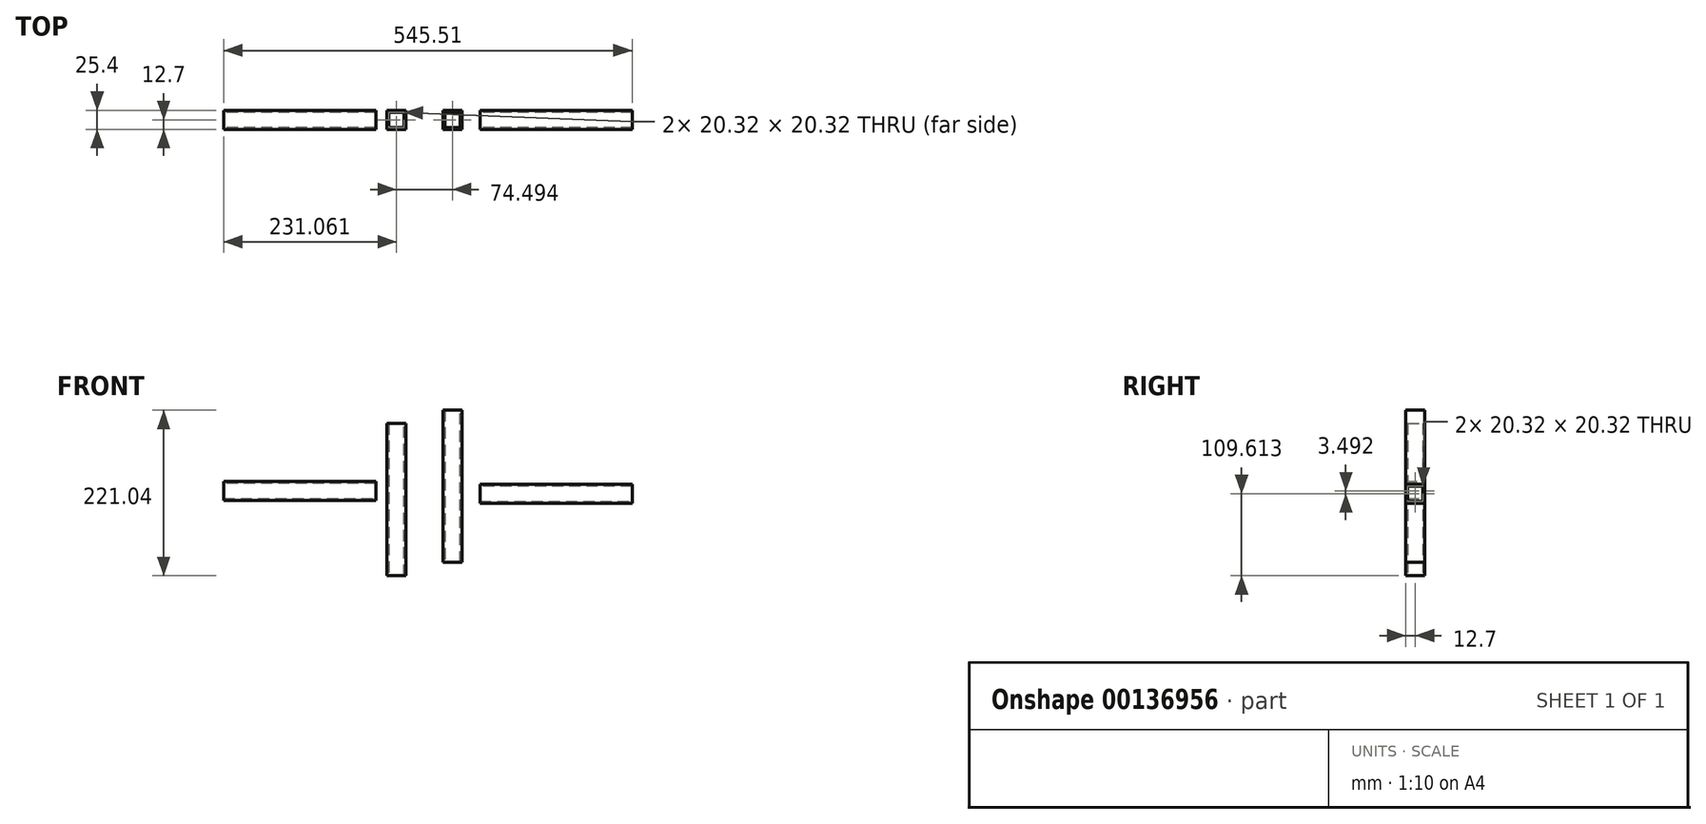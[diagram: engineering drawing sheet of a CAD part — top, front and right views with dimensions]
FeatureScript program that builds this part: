
annotation { "Feature Type Name" : "Feature", "Feature Type Description" : "" }
export const myFeature = defineFeature(function(context is Context, id is Id, definition is map)
    precondition{}
    {
        {
            var Q0;
            Q0=qCreatedBy(makeId("Front.planeOp"),FACE);
            var sketch = newSketch(context, id + "F0", { "sketchPlane" : qUnion([Q0])});
            skLineSegment(sketch, "E0", {"start": v(-59.04, 109.04) * mm, "end": v(-59.04, -94.16) * mm});
            skLineSegment(sketch, "E1", {"start": v(-59.04, -94.16) * mm, "end": v(-33.64, -94.16) * mm});
            skLineSegment(sketch, "E2", {"start": v(-33.64, -94.16) * mm, "end": v(-33.64, 109.04) * mm});
            skLineSegment(sketch, "E3", {"start": v(-33.64, 109.04) * mm, "end": v(-59.04, 109.04) * mm});
            skLineSegment(sketch, "E4", {"start": v(15.46, 126.88) * mm, "end": v(15.46, -76.32) * mm});
            skLineSegment(sketch, "E5", {"start": v(15.46, -76.32) * mm, "end": v(40.86, -76.32) * mm});
            skLineSegment(sketch, "E6", {"start": v(40.86, -76.32) * mm, "end": v(40.86, 126.88) * mm});
            skLineSegment(sketch, "E7", {"start": v(40.86, 126.88) * mm, "end": v(15.46, 126.88) * mm});
            skLineSegment(sketch, "E8", {"start": v(268.1, 28.15) * mm, "end": v(64.9, 28.15) * mm});
            skLineSegment(sketch, "E9", {"start": v(64.9, 28.15) * mm, "end": v(64.9, 2.75) * mm});
            skLineSegment(sketch, "E10", {"start": v(64.9, 2.75) * mm, "end": v(268.1, 2.75) * mm});
            skLineSegment(sketch, "E11", {"start": v(268.1, 28.15) * mm, "end": v(268.1, 2.75) * mm});
            skLineSegment(sketch, "E12", {"start": v(-74.2, 31.65) * mm, "end": v(-277.4, 31.65) * mm});
            skLineSegment(sketch, "E13", {"start": v(-277.4, 31.65) * mm, "end": v(-277.4, 6.25) * mm});
            skLineSegment(sketch, "E14", {"start": v(-277.4, 6.25) * mm, "end": v(-74.2, 6.25) * mm});
            skLineSegment(sketch, "E15", {"start": v(-74.2, 31.65) * mm, "end": v(-74.2, 6.25) * mm});
            skSolve(sketch);
        }
        {
            var Q0;
            Q0 = qSketchRegion(id + "F0", true);
            extrude(context, id + "F1", {"entities" : qUnion([Q0]), "depth" : 25.4 * mm});
        }
        {
            var Q0;
            Q0=makeQuery(id+"F1.opExtrude","SWEPT_FACE",FACE,{"disambiguationData":[OSD([sQuery(id+"F0.wireOp",EDGE,"E7")])]});
            var Q1;
            Q1=makeQuery(id+"F1.opExtrude","SWEPT_FACE",FACE,{"disambiguationData":[OSD([sQuery(id+"F0.wireOp",EDGE,"E3")])]});
            var Q2;
            Q2=makeQuery(id+"F1.opExtrude","SWEPT_FACE",FACE,{"disambiguationData":[OSD([sQuery(id+"F0.wireOp",EDGE,"E15")])]});
            var Q3;
            Q3=makeQuery(id+"F1.opExtrude","SWEPT_FACE",FACE,{"disambiguationData":[OSD([sQuery(id+"F0.wireOp",EDGE,"E11")])]});
            var Q4;
            Q4=makeQuery(id+"F1.opExtrude","SWEPT_FACE",FACE,{"disambiguationData":[OSD([sQuery(id+"F0.wireOp",EDGE,"E1")])]});
            var Q5;
            Q5=makeQuery(id+"F1.opExtrude","SWEPT_FACE",FACE,{"disambiguationData":[OSD([sQuery(id+"F0.wireOp",EDGE,"E5")])]});
            var Q6;
            Q6=makeQuery(id+"F1.opExtrude","SWEPT_FACE",FACE,{"disambiguationData":[OSD([sQuery(id+"F0.wireOp",EDGE,"E9")])]});
            var Q7;
            Q7=makeQuery(id+"F1.opExtrude","SWEPT_FACE",FACE,{"disambiguationData":[OSD([sQuery(id+"F0.wireOp",EDGE,"E13")])]});
            shell(context, id + "F2", {"entities" : qUnion([Q0, Q1, Q2, Q3, Q4, Q5, Q6, Q7]), "thickness" : 2.54 * mm});
        }
    });
